# Revit family: Hitachi_RAS-S50_S60_S70_S80YHA_0718
name_source: partatom
category: Mechanical Equipment
revit_build: Autodesk Revit 2015 (Build: 20140223_1515(x64)
units: mm (PartAtom-declared; Revit-internal decimal feet)

## types (4) — shared parameters
Depth = 260 mm  [stored 0.853018 ft]
Height = 300 mm
Manufacturer = Hitachi
Pip Connection Size - Liquid = 6.40 mm
Pipe Connection Size - Gas = 12.70 mm
Pipe Height (max.) = 20m
Pipe Length (min./max.) = 3m to 30m
URL = www.temperzone.biz
Weight (kg) = 15
Width = 1100 mm

## per-type parameters (varying)
| type | Cooling Capacity | Cooling Range (kW) | Description | Heating Capacity | Heating Range (kW) | Model - Outdoor |
| RAS-S80YHA | 8 kW | 1.5 kW to 8.5 kW | Hitachi Wall Mounted 8.0kW Heatpump RAS-S80YHA | 9 kW | 1.5 kW to 9.5 kW | RAC-S80YHA |
| RAS-S70YHA | 7 kW | 1.5 kW to 8.0 kW | Hitachi Wall Mounted 7.0kW Heatpump RAS-S70YHA | 8 kW | 1.5 kW to 8.5 kW | RAC-S70YHA |
| RAS-S50YHA | 5 kW | 1.2 kW to 5.8 kW | Hitachi Wall Mounted 5.0kW Heatpump RAS-S50YHA | 6 kW | 1.2 kW to 6.8 kW | RAC-S50YHA |
| RAS-S60YHA | 5 kW | 1.2 kW to 6.5 kW | Hitachi Wall Mounted 5.0kW Heatpump RAS-S60YHA | 6 kW | 1.2 kW to 8.0 kW | RAC-S60YHA |

note: column(s) folded — value = type name in every type: Model

note: [stored X ft] marks values corroborated as IEEE doubles in the binary element streams (Revit-internal decimal feet)

## geometry (parser evidence)
native form markers: Blend x6, Sweep x6
no freeform markers — native parametric forms only
